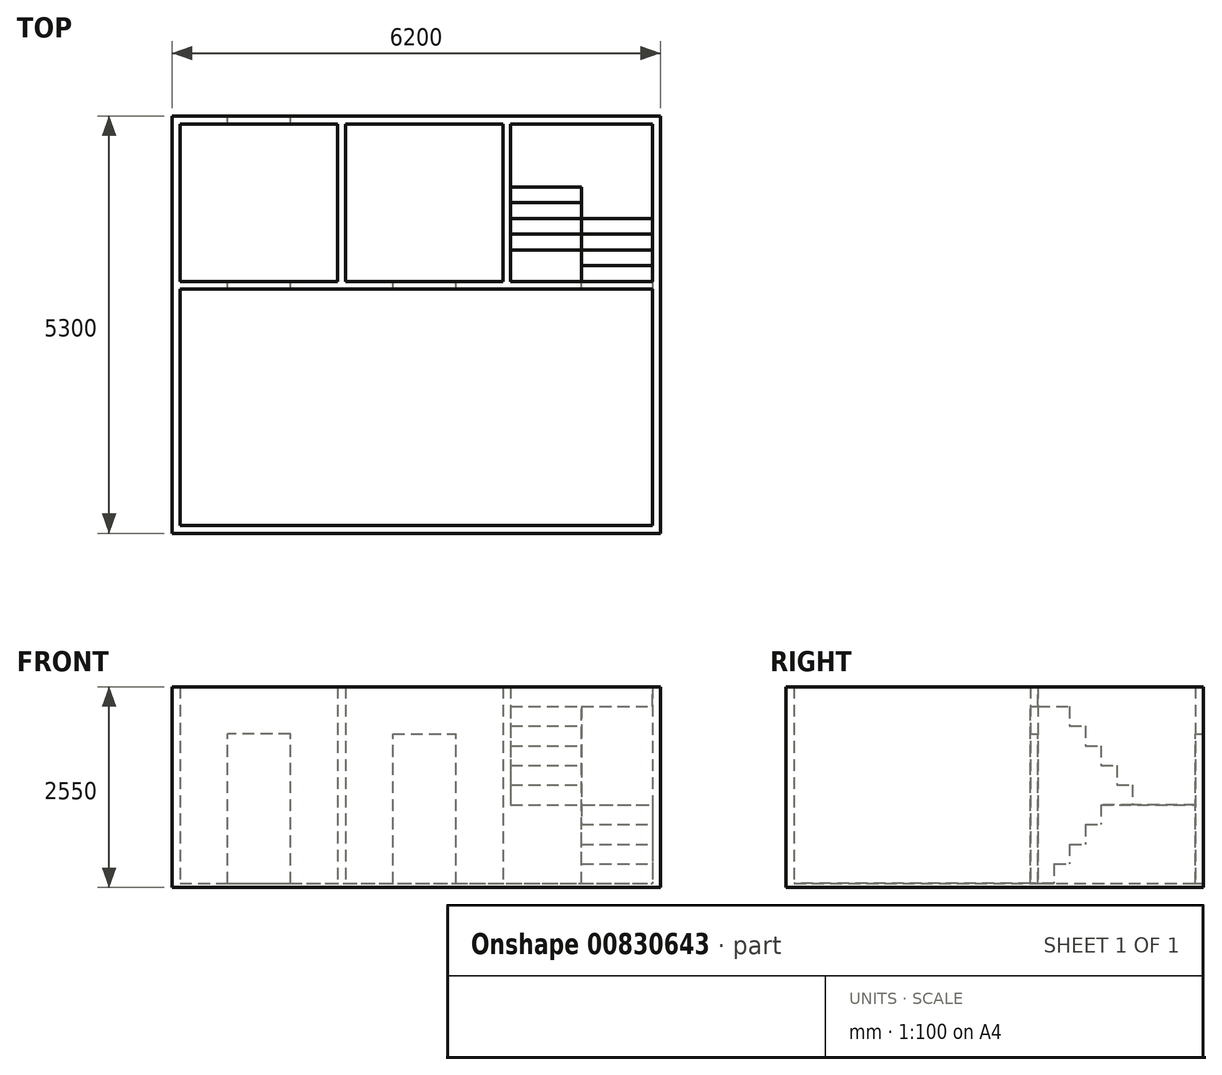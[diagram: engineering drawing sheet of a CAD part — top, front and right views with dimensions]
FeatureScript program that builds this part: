
annotation { "Feature Type Name" : "Feature", "Feature Type Description" : "" }
export const myFeature = defineFeature(function(context is Context, id is Id, definition is map)
    precondition{}
    {
        {
            var Q0;
            Q0=qCreatedBy(makeId("Top.planeOp"),FACE);
            var sketch = newSketch(context, id + "F0", { "sketchPlane" : qUnion([Q0])});
            skLineSegment(sketch, "E0.bottom", {"start": v(-1956.14, 1822.74) * mm, "end": v(43.86, 1822.74) * mm});
            skLineSegment(sketch, "E0.top", {"start": v(-1956.14, -177.26) * mm, "end": v(43.86, -177.26) * mm});
            skLineSegment(sketch, "E0.left", {"start": v(-1956.14, 1822.74) * mm, "end": v(-1956.14, -177.26) * mm});
            skLineSegment(sketch, "E0.right", {"start": v(43.86, 1822.74) * mm, "end": v(43.86, -177.26) * mm});
            skLineSegment(sketch, "E1", {"start": v(-1956.14, 1822.74) * mm, "end": v(-1956.14, 1922.74) * mm});
            skLineSegment(sketch, "E2", {"start": v(-1956.14, 1922.74) * mm, "end": v(-1956.14, 1822.74) * mm});
            skLineSegment(sketch, "E3", {"start": v(-1956.14, 1822.74) * mm, "end": v(-2056.14, 1822.74) * mm});
            skLineSegment(sketch, "E4.bottom", {"start": v(-2056.14, 1922.74) * mm, "end": v(143.86, 1922.74) * mm});
            skLineSegment(sketch, "E4.top", {"start": v(-2056.14, -277.26) * mm, "end": v(143.86, -277.26) * mm});
            skLineSegment(sketch, "E4.left", {"start": v(-2056.14, 1922.74) * mm, "end": v(-2056.14, -277.26) * mm});
            skLineSegment(sketch, "E4.right", {"start": v(143.86, 1922.74) * mm, "end": v(143.86, -277.26) * mm});
            skLineSegment(sketch, "E5.bottom", {"start": v(-1956.14, -277.26) * mm, "end": v(4043.86, -277.26) * mm});
            skLineSegment(sketch, "E5.top", {"start": v(-1956.14, -3277.26) * mm, "end": v(4043.86, -3277.26) * mm});
            skLineSegment(sketch, "E5.left", {"start": v(-1956.14, -277.26) * mm, "end": v(-1956.14, -3277.26) * mm});
            skLineSegment(sketch, "E5.right", {"start": v(4043.86, -277.26) * mm, "end": v(4043.86, -3277.26) * mm});
            skLineSegment(sketch, "E6.bottom", {"start": v(-2056.14, -177.26) * mm, "end": v(4143.86, -177.26) * mm});
            skLineSegment(sketch, "E6.top", {"start": v(-2056.14, -3377.26) * mm, "end": v(4143.86, -3377.26) * mm});
            skLineSegment(sketch, "E6.left", {"start": v(-2056.14, -177.26) * mm, "end": v(-2056.14, -3377.26) * mm});
            skLineSegment(sketch, "E6.right", {"start": v(4143.86, -177.26) * mm, "end": v(4143.86, -3377.26) * mm});
            skPoint(sketch, "E7.firstSnap0", {"position": v(1043.86, -177.26) * mm});
            skLineSegment(sketch, "E7.bottom", {"start": v(143.86, -177.26) * mm, "end": v(2143.86, -177.26) * mm});
            skLineSegment(sketch, "E7.top", {"start": v(143.86, 1822.74) * mm, "end": v(2143.86, 1822.74) * mm});
            skLineSegment(sketch, "E7.left", {"start": v(143.86, -177.26) * mm, "end": v(143.86, 1822.74) * mm});
            skLineSegment(sketch, "E7.right", {"start": v(2143.86, -177.26) * mm, "end": v(2143.86, 1822.74) * mm});
            skLineSegment(sketch, "E8.bottom", {"start": v(143.86, 1922.74) * mm, "end": v(2243.86, 1922.74) * mm});
            skLineSegment(sketch, "E8.top", {"start": v(143.86, -177.26) * mm, "end": v(2243.86, -177.26) * mm});
            skLineSegment(sketch, "E8.left", {"start": v(143.86, 1922.74) * mm, "end": v(143.86, -177.26) * mm});
            skLineSegment(sketch, "E8.right", {"start": v(2243.86, 1922.74) * mm, "end": v(2243.86, -177.26) * mm});
            skLineSegment(sketch, "E9.bottom", {"start": v(2243.86, 1922.74) * mm, "end": v(4143.86, 1922.74) * mm});
            skLineSegment(sketch, "E9.top", {"start": v(2243.86, -177.26) * mm, "end": v(4143.86, -177.26) * mm});
            skLineSegment(sketch, "E9.right", {"start": v(4143.86, 1922.74) * mm, "end": v(4143.86, -177.26) * mm});
            skLineSegment(sketch, "E10.bottom", {"start": v(2243.86, 1822.74) * mm, "end": v(4043.86, 1822.74) * mm});
            skLineSegment(sketch, "E10.left", {"start": v(2243.86, 1822.74) * mm, "end": v(2243.86, -177.26) * mm});
            skLineSegment(sketch, "E10.right", {"start": v(4043.86, 1822.74) * mm, "end": v(4043.86, -177.26) * mm});
            skLineSegment(sketch, "E11", {"start": v(2243.86, -177.26) * mm, "end": v(2243.86, -277.26) * mm});
            skLineSegment(sketch, "E12", {"start": v(4043.86, -277.26) * mm, "end": v(4043.86, -177.26) * mm});
            skLineSegment(sketch, "E13", {"start": v(4143.86, 1922.74) * mm, "end": v(4143.86, 2321.86) * mm});
            skLineSegment(sketch, "E14", {"start": v(4143.86, 2321.86) * mm, "end": v(3143.86, 2321.86) * mm});
            skLineSegment(sketch, "E15", {"start": v(3143.86, 2321.86) * mm, "end": v(3143.86, -177.26) * mm});
            skSolve(sketch);
        }
        {
            var Q0;
            Q0=makeQuery(id+"F0.imprint","IMPRINT",FACE,{"disambiguationData":[TD([[makeQuery(id+"F0.imprint","IMPRINT",EDGE,{"derivedFrom":sQuery(id+"F0.wireOp",EDGE,"E0.bottom")}),1.0]])]});
            var Q1;
            {var subQ0=sQuery(id+"F0.wireOp",EDGE,"E1");Q1=makeQuery(id+"F0.imprint","IMPRINT",FACE,{"disambiguationData":[TD([[makeQuery(id+"F0.imprint","IMPRINT",EDGE,{"derivedFrom":subQ0}),1.0]])]});}
            var Q2;
            {var subQ2=sQuery(id+"F0.wireOp",EDGE,"E11");Q2=makeQuery(id+"F0.imprint","IMPRINT",FACE,{"disambiguationData":[TD([[makeQuery(id+"F0.imprint","IMPRINT",EDGE,{"derivedFrom":subQ2}),-1.0]])]});}
            var Q3;
            {var subQ1=sQuery(id+"F0.wireOp",EDGE,"E7.top");Q3=makeQuery(id+"F0.imprint","IMPRINT",FACE,{"disambiguationData":[TD([[makeQuery(id+"F0.imprint","IMPRINT",EDGE,{"derivedFrom":subQ1}),1.0]])]});}
            var Q4;
            {var subQ0=sQuery(id+"F0.wireOp",EDGE,"E0.left");Q4=makeQuery(id+"F0.imprint","IMPRINT",FACE,{"disambiguationData":[TD([[makeQuery(id+"F0.imprint","IMPRINT",EDGE,{"derivedFrom":subQ0}),-1.0]])]});}
            var Q5;
            {var subQ8=sQuery(id+"F0.wireOp",EDGE,"E0.top");Q5=makeQuery(id+"F0.imprint","IMPRINT",FACE,{"disambiguationData":[TD([[makeQuery(id+"F0.imprint","IMPRINT",EDGE,{"derivedFrom":subQ8}),-1.0]])]});}
            var Q6;
            Q6=makeQuery(id+"F0.imprint","IMPRINT",FACE,{"disambiguationData":[TD([[makeQuery(id+"F0.imprint","IMPRINT",EDGE,{"derivedFrom":sQuery(id+"F0.wireOp",EDGE,"E5.top")}),-1.0]])]});
            var Q7;
            {var subQ1=sQuery(id+"F0.wireOp",EDGE,"E8.right");var subQ3=sQuery(id+"F0.wireOp",EDGE,"E10.bottom");var subQ4=makeQuery(id+"F0.imprint","INTERSECT",VERTEX,{"derivedFrom":[subQ1,subQ3]});Q7=makeQuery(id+"F0.imprint","IMPRINT",FACE,{"disambiguationData":[TD([[makeQuery(id+"F0.imprint","IMPRINT",EDGE,{"disambiguationData":[TD([[subQ4,-1.0]])],"derivedFrom":subQ3}),1.0]])]});}
            var Q8;
            {var subQ0=sQuery(id+"F0.wireOp",EDGE,"E9.right");Q8=makeQuery(id+"F0.imprint","IMPRINT",FACE,{"disambiguationData":[TD([[makeQuery(id+"F0.imprint","IMPRINT",EDGE,{"derivedFrom":subQ0}),-1.0]])]});}
            extrude(context, id + "F1", {"entities" : qUnion([Q0, Q1, Q2, Q3, Q4, Q5, Q6, Q7, Q8]), "depth" : 2500 * mm, "offsetDistance" : 25 * mm});
        }
        {
            var Q0;
            Q0=qCreatedBy(makeId("Front.planeOp"),FACE);
            var sketch = newSketch(context, id + "F2", { "sketchPlane" : qUnion([Q0])});
            skLineSegment(sketch, "E16", {"start": v(4144.79, 0) * mm, "end": v(-2052.73, 0) * mm});
            skLineSegment(sketch, "E17", {"start": v(-2052.73, 0) * mm, "end": v(-1352.73, 0) * mm});
            skLineSegment(sketch, "E18", {"start": v(-1352.73, 0) * mm, "end": v(-552.73, 0) * mm});
            skLineSegment(sketch, "E19", {"start": v(-552.73, 0) * mm, "end": v(147.27, 0) * mm});
            skLineSegment(sketch, "E20.bottom", {"start": v(-552.73, 0) * mm, "end": v(-1352.73, 0) * mm});
            skLineSegment(sketch, "E20.top", {"start": v(-552.73, 1900) * mm, "end": v(-1352.73, 1900) * mm});
            skLineSegment(sketch, "E20.left", {"start": v(-552.73, 0) * mm, "end": v(-552.73, 1900) * mm});
            skLineSegment(sketch, "E20.right", {"start": v(-1352.73, 0) * mm, "end": v(-1352.73, 1900) * mm});
            skLineSegment(sketch, "E21", {"start": v(147.27, 0) * mm, "end": v(747.27, 0) * mm});
            skLineSegment(sketch, "E22.bottom", {"start": v(747.27, 0) * mm, "end": v(1547.27, 0) * mm});
            skLineSegment(sketch, "E22.top", {"start": v(747.27, 1900) * mm, "end": v(1547.27, 1900) * mm});
            skLineSegment(sketch, "E22.left", {"start": v(747.27, 0) * mm, "end": v(747.27, 1900) * mm});
            skLineSegment(sketch, "E22.right", {"start": v(1547.27, 0) * mm, "end": v(1547.27, 1900) * mm});
            skSolve(sketch);
        }
        {
            var Q0;
            Q0=makeQuery(id+"F2.imprint","IMPRINT",FACE,{"disambiguationData":[TD([[makeQuery(id+"F2.imprint","IMPRINT",EDGE,{"derivedFrom":sQuery(id+"F2.wireOp",EDGE,"E20.top")}),1.0]])]});
            extrude(context, id + "F3", {"entities" : qUnion([Q0]), "operationType" : NewBodyOperationType.REMOVE, "endBound" : BoundingType.SYMMETRIC, "depth" : 4140 * mm, "offsetDistance" : 25 * mm});
        }
        {
            var Q0;
            Q0=makeQuery(id+"F2.imprint","IMPRINT",FACE,{"disambiguationData":[TD([[makeQuery(id+"F2.imprint","IMPRINT",EDGE,{"derivedFrom":sQuery(id+"F2.wireOp",EDGE,"E22.top")}),-1.0]])]});
            extrude(context, id + "F4", {"entities" : qUnion([Q0]), "operationType" : NewBodyOperationType.REMOVE, "depth" : 1630 * mm, "offsetDistance" : 25 * mm});
        }
        {
            var Q0;
            Q0=makeQuery(id+"F1.opExtrude","SWEPT_FACE",FACE,{"disambiguationData":[OSD([sQuery(id+"F0.wireOp",EDGE,"E6.right"),sQuery(id+"F0.wireOp",EDGE,"E9.right")])]});
            cPlane(context, id + "F5", {"entities" : qUnion([Q0]), "cplaneType" : CPlaneType.OFFSET, "offset" : 0 * mm, "width" : 150 * mm, "height" : 150 * mm});
        }
        {
            var Q0;
            Q0=makeQuery(id+"F0.imprint","IMPRINT",FACE,{"disambiguationData":[TD([[makeQuery(id+"F0.imprint","IMPRINT",EDGE,{"derivedFrom":sQuery(id+"F0.wireOp",EDGE,"E5.top")}),-1.0]])]});
            var sketch = newSketch(context, id + "F6", { "sketchPlane" : qUnion([Q0])});
            skLineSegment(sketch, "E23.bottom", {"start": v(-2056.14, -3377.26) * mm, "end": v(4143.86, -3377.26) * mm});
            skLineSegment(sketch, "E23.top", {"start": v(-2056.14, 1922.74) * mm, "end": v(4143.86, 1922.74) * mm});
            skLineSegment(sketch, "E23.left", {"start": v(-2056.14, -3377.26) * mm, "end": v(-2056.14, 1922.74) * mm});
            skLineSegment(sketch, "E23.right", {"start": v(4143.86, -3377.26) * mm, "end": v(4143.86, 1922.74) * mm});
            skSolve(sketch);
        }
        {
            var Q0;
            Q0 = qSketchRegion(id + "F6", true);
            extrude(context, id + "F7", {"entities" : qUnion([Q0]), "operationType" : NewBodyOperationType.ADD, "oppositeDirection" : true, "depth" : 50 * mm, "offsetDistance" : 25 * mm});
        }
        {
            var Q0;
            Q0=qCreatedBy(id+"F5.planeOp",FACE);
            var sketch = newSketch(context, id + "F8", { "sketchPlane" : qUnion([Q0])});
            skLineSegment(sketch, "E24", {"start": v(1922.74, 0) * mm, "end": v(-3377.26, 0) * mm});
            skLineSegment(sketch, "E25", {"start": v(1922.74, 0) * mm, "end": v(1822.74, 0) * mm});
            skLineSegment(sketch, "E26", {"start": v(1822.74, 0) * mm, "end": v(-177.26, 0) * mm});
            skLineSegment(sketch, "E27", {"start": v(1822.74, 0) * mm, "end": v(1822.74, 2500) * mm});
            skLineSegment(sketch, "E28.bottom", {"start": v(1822.74, 0) * mm, "end": v(22.74, 0) * mm});
            skLineSegment(sketch, "E28.top", {"start": v(1822.74, 250) * mm, "end": v(22.74, 250) * mm});
            skLineSegment(sketch, "E28.left", {"start": v(1822.74, 0) * mm, "end": v(1822.74, 250) * mm});
            skLineSegment(sketch, "E28.right", {"start": v(22.74, 0) * mm, "end": v(22.74, 250) * mm});
            skLineSegment(sketch, "E29.bottom", {"start": v(1822.74, 250) * mm, "end": v(222.74, 250) * mm});
            skLineSegment(sketch, "E29.top", {"start": v(1822.74, 500) * mm, "end": v(222.74, 500) * mm});
            skLineSegment(sketch, "E29.left", {"start": v(1822.74, 250) * mm, "end": v(1822.74, 500) * mm});
            skLineSegment(sketch, "E29.right", {"start": v(222.74, 250) * mm, "end": v(222.74, 500) * mm});
            skLineSegment(sketch, "E30.bottom", {"start": v(1822.74, 500) * mm, "end": v(422.74, 500) * mm});
            skLineSegment(sketch, "E30.top", {"start": v(1822.74, 750) * mm, "end": v(422.74, 750) * mm});
            skLineSegment(sketch, "E30.left", {"start": v(1822.74, 500) * mm, "end": v(1822.74, 750) * mm});
            skLineSegment(sketch, "E30.right", {"start": v(422.74, 500) * mm, "end": v(422.74, 750) * mm});
            skLineSegment(sketch, "E31.bottom", {"start": v(1822.74, 750) * mm, "end": v(622.74, 750) * mm});
            skLineSegment(sketch, "E31.top", {"start": v(1822.74, 1000) * mm, "end": v(622.74, 1000) * mm});
            skLineSegment(sketch, "E31.left", {"start": v(1822.74, 750) * mm, "end": v(1822.74, 1000) * mm});
            skLineSegment(sketch, "E31.right", {"start": v(622.74, 750) * mm, "end": v(622.74, 1000) * mm});
            skLineSegment(sketch, "E32", {"start": v(-177.26, 0) * mm, "end": v(-177.26, 2500) * mm});
            skLineSegment(sketch, "E33.bottom", {"start": v(-177.26, 2500) * mm, "end": v(22.74, 2500) * mm});
            skLineSegment(sketch, "E33.top", {"start": v(-177.26, 2250) * mm, "end": v(22.74, 2250) * mm});
            skLineSegment(sketch, "E33.left", {"start": v(-177.26, 2500) * mm, "end": v(-177.26, 2250) * mm});
            skLineSegment(sketch, "E33.right", {"start": v(22.74, 2500) * mm, "end": v(22.74, 2250) * mm});
            skLineSegment(sketch, "E34.bottom", {"start": v(-177.26, 2250) * mm, "end": v(222.74, 2250) * mm});
            skLineSegment(sketch, "E34.top", {"start": v(-177.26, 2000) * mm, "end": v(222.74, 2000) * mm});
            skLineSegment(sketch, "E34.left", {"start": v(-177.26, 2250) * mm, "end": v(-177.26, 2000) * mm});
            skLineSegment(sketch, "E34.right", {"start": v(222.74, 2250) * mm, "end": v(222.74, 2000) * mm});
            skLineSegment(sketch, "E35.bottom", {"start": v(-177.26, 2000) * mm, "end": v(422.74, 2000) * mm});
            skLineSegment(sketch, "E35.top", {"start": v(-177.26, 1750) * mm, "end": v(422.74, 1750) * mm});
            skLineSegment(sketch, "E35.left", {"start": v(-177.26, 2000) * mm, "end": v(-177.26, 1750) * mm});
            skLineSegment(sketch, "E35.right", {"start": v(422.74, 2000) * mm, "end": v(422.74, 1750) * mm});
            skLineSegment(sketch, "E36.bottom", {"start": v(-177.26, 1750) * mm, "end": v(622.74, 1750) * mm});
            skLineSegment(sketch, "E36.top", {"start": v(-177.26, 1500) * mm, "end": v(622.74, 1500) * mm});
            skLineSegment(sketch, "E36.left", {"start": v(-177.26, 1750) * mm, "end": v(-177.26, 1500) * mm});
            skLineSegment(sketch, "E36.right", {"start": v(622.74, 1750) * mm, "end": v(622.74, 1500) * mm});
            skLineSegment(sketch, "E37.bottom", {"start": v(-177.26, 1500) * mm, "end": v(822.74, 1500) * mm});
            skLineSegment(sketch, "E37.top", {"start": v(-177.26, 1250) * mm, "end": v(822.74, 1250) * mm});
            skLineSegment(sketch, "E37.left", {"start": v(-177.26, 1500) * mm, "end": v(-177.26, 1250) * mm});
            skLineSegment(sketch, "E37.right", {"start": v(822.74, 1500) * mm, "end": v(822.74, 1250) * mm});
            skLineSegment(sketch, "E38.bottom", {"start": v(-177.26, 1250) * mm, "end": v(1022.74, 1250) * mm});
            skLineSegment(sketch, "E38.top", {"start": v(-177.26, 1000) * mm, "end": v(1022.74, 1000) * mm});
            skLineSegment(sketch, "E38.left", {"start": v(-177.26, 1250) * mm, "end": v(-177.26, 1000) * mm});
            skLineSegment(sketch, "E38.right", {"start": v(1022.74, 1250) * mm, "end": v(1022.74, 1000) * mm});
            skSolve(sketch);
        }
        {
            var Q0;
            {var subQ4=sQuery(id+"F8.wireOp",EDGE,"E28.right");Q0=makeQuery(id+"F8.imprint","IMPRINT",FACE,{"disambiguationData":[TD([[makeQuery(id+"F8.imprint","IMPRINT",EDGE,{"derivedFrom":subQ4}),-1.0]])]});}
            var Q1;
            {var subQ6=sQuery(id+"F8.wireOp",EDGE,"E29.right");Q1=makeQuery(id+"F8.imprint","IMPRINT",FACE,{"disambiguationData":[TD([[makeQuery(id+"F8.imprint","IMPRINT",EDGE,{"derivedFrom":subQ6}),-1.0]])]});}
            var Q2;
            {var subQ6=sQuery(id+"F8.wireOp",EDGE,"E30.right");Q2=makeQuery(id+"F8.imprint","IMPRINT",FACE,{"disambiguationData":[TD([[makeQuery(id+"F8.imprint","IMPRINT",EDGE,{"derivedFrom":subQ6}),-1.0]])]});}
            extrude(context, id + "F9", {"entities" : qUnion([Q0, Q1, Q2]), "operationType" : NewBodyOperationType.ADD, "oppositeDirection" : true, "depth" : 1000 * mm, "offsetDistance" : 25 * mm});
        }
        {
            var Q0;
            {var subQ0=sQuery(id+"F8.wireOp",EDGE,"E31.right");Q0=makeQuery(id+"F8.imprint","IMPRINT",FACE,{"disambiguationData":[TD([[makeQuery(id+"F8.imprint","IMPRINT",EDGE,{"derivedFrom":subQ0}),-1.0]])]});}
            extrude(context, id + "F10", {"entities" : qUnion([Q0]), "operationType" : NewBodyOperationType.ADD, "oppositeDirection" : true, "depth" : 1900 * mm, "offsetDistance" : 25 * mm});
        }
        {
            var Q0;
            {var subQ0=sQuery(id+"F8.wireOp",EDGE,"E33.bottom");Q0=makeQuery(id+"F8.imprint","IMPRINT",FACE,{"disambiguationData":[TD([[makeQuery(id+"F8.imprint","IMPRINT",EDGE,{"derivedFrom":subQ0}),-1.0]])]});}
            var Q1;
            {var subQ1=sQuery(id+"F8.wireOp",EDGE,"E33.top");Q1=makeQuery(id+"F8.imprint","IMPRINT",FACE,{"disambiguationData":[TD([[makeQuery(id+"F8.imprint","IMPRINT",EDGE,{"derivedFrom":subQ1}),-1.0]])]});}
            var Q2;
            {var subQ1=sQuery(id+"F8.wireOp",EDGE,"E34.top");Q2=makeQuery(id+"F8.imprint","IMPRINT",FACE,{"disambiguationData":[TD([[makeQuery(id+"F8.imprint","IMPRINT",EDGE,{"derivedFrom":subQ1}),-1.0]])]});}
            var Q3;
            {var subQ1=sQuery(id+"F8.wireOp",EDGE,"E35.top");Q3=makeQuery(id+"F8.imprint","IMPRINT",FACE,{"disambiguationData":[TD([[makeQuery(id+"F8.imprint","IMPRINT",EDGE,{"derivedFrom":subQ1}),-1.0]])]});}
            var Q4;
            {var subQ1=sQuery(id+"F8.wireOp",EDGE,"E36.top");Q4=makeQuery(id+"F8.imprint","IMPRINT",FACE,{"disambiguationData":[TD([[makeQuery(id+"F8.imprint","IMPRINT",EDGE,{"derivedFrom":subQ1}),-1.0]])]});}
            var Q5;
            {var subQ0=sQuery(id+"F8.wireOp",EDGE,"E37.top");Q5=makeQuery(id+"F8.imprint","IMPRINT",FACE,{"disambiguationData":[TD([[makeQuery(id+"F8.imprint","IMPRINT",EDGE,{"derivedFrom":subQ0}),-1.0]])]});}
            extrude(context, id + "F11", {"entities" : qUnion([Q0, Q1, Q2, Q3, Q4, Q5]), "operationType" : NewBodyOperationType.ADD, "oppositeDirection" : true, "depth" : 1900 * mm, "offsetDistance" : 25 * mm});
        }
        {
            var Q0;
            {var subQ1=sQuery(id+"F8.wireOp",EDGE,"E33.top");Q0=makeQuery(id+"F8.imprint","IMPRINT",FACE,{"disambiguationData":[TD([[makeQuery(id+"F8.imprint","IMPRINT",EDGE,{"derivedFrom":subQ1}),-1.0]])]});}
            var Q1;
            {var subQ1=sQuery(id+"F8.wireOp",EDGE,"E34.top");Q1=makeQuery(id+"F8.imprint","IMPRINT",FACE,{"disambiguationData":[TD([[makeQuery(id+"F8.imprint","IMPRINT",EDGE,{"derivedFrom":subQ1}),-1.0]])]});}
            var Q2;
            {var subQ1=sQuery(id+"F8.wireOp",EDGE,"E35.top");Q2=makeQuery(id+"F8.imprint","IMPRINT",FACE,{"disambiguationData":[TD([[makeQuery(id+"F8.imprint","IMPRINT",EDGE,{"derivedFrom":subQ1}),-1.0]])]});}
            var Q3;
            {var subQ1=sQuery(id+"F8.wireOp",EDGE,"E36.top");Q3=makeQuery(id+"F8.imprint","IMPRINT",FACE,{"disambiguationData":[TD([[makeQuery(id+"F8.imprint","IMPRINT",EDGE,{"derivedFrom":subQ1}),-1.0]])]});}
            var Q4;
            {var subQ0=sQuery(id+"F8.wireOp",EDGE,"E37.top");Q4=makeQuery(id+"F8.imprint","IMPRINT",FACE,{"disambiguationData":[TD([[makeQuery(id+"F8.imprint","IMPRINT",EDGE,{"derivedFrom":subQ0}),-1.0]])]});}
            extrude(context, id + "F12", {"entities" : qUnion([Q0, Q1, Q2, Q3, Q4]), "operationType" : NewBodyOperationType.REMOVE, "oppositeDirection" : true, "depth" : 1000 * mm, "offsetDistance" : 25 * mm});
        }
        {
            var Q0;
            Q0=makeQuery(id+"F12.boolean.opBoolean","COPY",FACE,{"derivedFrom":makeQuery(id+"F12.opExtrude","SWEPT_FACE",FACE,{"disambiguationData":[OSD([sQuery(id+"F8.wireOp",EDGE,"E32")])]})});
            extrude(context, id + "F13", {"entities" : qUnion([Q0]), "operationType" : NewBodyOperationType.ADD, "depth" : 1480 * mm, "offsetDistance" : 25 * mm});
        }
        {
            var Q0;
            {var subQ0=sQuery(id+"F0.wireOp",EDGE,"E8.right");var subQ5=sQuery(id+"F0.wireOp",EDGE,"E10.bottom");var subQ6=makeQuery(id+"F0.imprint","INTERSECT",VERTEX,{"derivedFrom":[subQ0,subQ5]});Q0=makeQuery(id+"F0.imprint","IMPRINT",FACE,{"disambiguationData":[TD([[makeQuery(id+"F0.imprint","IMPRINT",EDGE,{"disambiguationData":[TD([[subQ6,-1.0]])],"derivedFrom":subQ5}),-1.0]])]});}
            extrude(context, id + "F14", {"entities" : qUnion([Q0]), "operationType" : NewBodyOperationType.ADD, "depth" : 1000 * mm, "offsetDistance" : 25 * mm});
        }
        {
            var Q0;
            Q0=makeQuery(id+"F14.boolean.opBoolean","MERGE",FACE,{"derivedFrom":[makeQuery(id+"F11.opExtrude","SWEPT_FACE",FACE,{"disambiguationData":[OSD([sQuery(id+"F8.wireOp",EDGE,"E32")])]}),makeQuery(id+"F14.opExtrude","SWEPT_FACE",FACE,{"disambiguationData":[OSD([sQuery(id+"F0.wireOp",EDGE,"E6.bottom")])]})]});
            extrude(context, id + "F15", {"entities" : qUnion([Q0]), "operationType" : NewBodyOperationType.ADD, "depth" : 100 * mm, "offsetDistance" : 25 * mm});
        }
        {
            var Q0;
            Q0=makeQuery(id+"F11.opExtrude","SWEPT_FACE",FACE,{"disambiguationData":[OSD([sQuery(id+"F8.wireOp",EDGE,"E33.right")])]});
            var sketch = newSketch(context, id + "F16", { "sketchPlane" : qUnion([Q0])});
            skLineSegment(sketch, "E39", {"start": v(-4043.86, 2333.61) * mm, "end": v(-2243.86, 2333.61) * mm});
            skLineSegment(sketch, "E40", {"start": v(-2243.86, 2333.61) * mm, "end": v(-3143.86, 2333.61) * mm});
            skLineSegment(sketch, "E41", {"start": v(-3143.86, 2333.61) * mm, "end": v(-3143.86, 2500) * mm});
            skLineSegment(sketch, "E42", {"start": v(-3143.86, 2500) * mm, "end": v(-3143.86, 2250) * mm});
            skLineSegment(sketch, "E43.bottom", {"start": v(-3143.86, 2250) * mm, "end": v(-4043.86, 2250) * mm});
            skLineSegment(sketch, "E43.top", {"start": v(-3143.86, 2500) * mm, "end": v(-4043.86, 2500) * mm});
            skLineSegment(sketch, "E43.left", {"start": v(-3143.86, 2250) * mm, "end": v(-3143.86, 2500) * mm});
            skLineSegment(sketch, "E43.right", {"start": v(-4043.86, 2250) * mm, "end": v(-4043.86, 2500) * mm});
            skSolve(sketch);
        }
        {
            var Q0;
            {var subQ0=sQuery(id+"F16.wireOp",EDGE,"E39");Q0=makeQuery(id+"F16.imprint","IMPRINT",FACE,{"disambiguationData":[TD([[makeQuery(id+"F16.imprint","IMPRINT",EDGE,{"derivedFrom":subQ0}),1.0]])]});}
            var Q1;
            {var subQ0=sQuery(id+"F16.wireOp",EDGE,"E39");Q1=makeQuery(id+"F16.imprint","IMPRINT",FACE,{"disambiguationData":[TD([[makeQuery(id+"F16.imprint","IMPRINT",EDGE,{"derivedFrom":subQ0}),-1.0]])]});}
            extrude(context, id + "F17", {"entities" : qUnion([Q0, Q1]), "operationType" : NewBodyOperationType.REMOVE, "oppositeDirection" : true, "depth" : 200 * mm, "offsetDistance" : 25 * mm});
        }
    });
